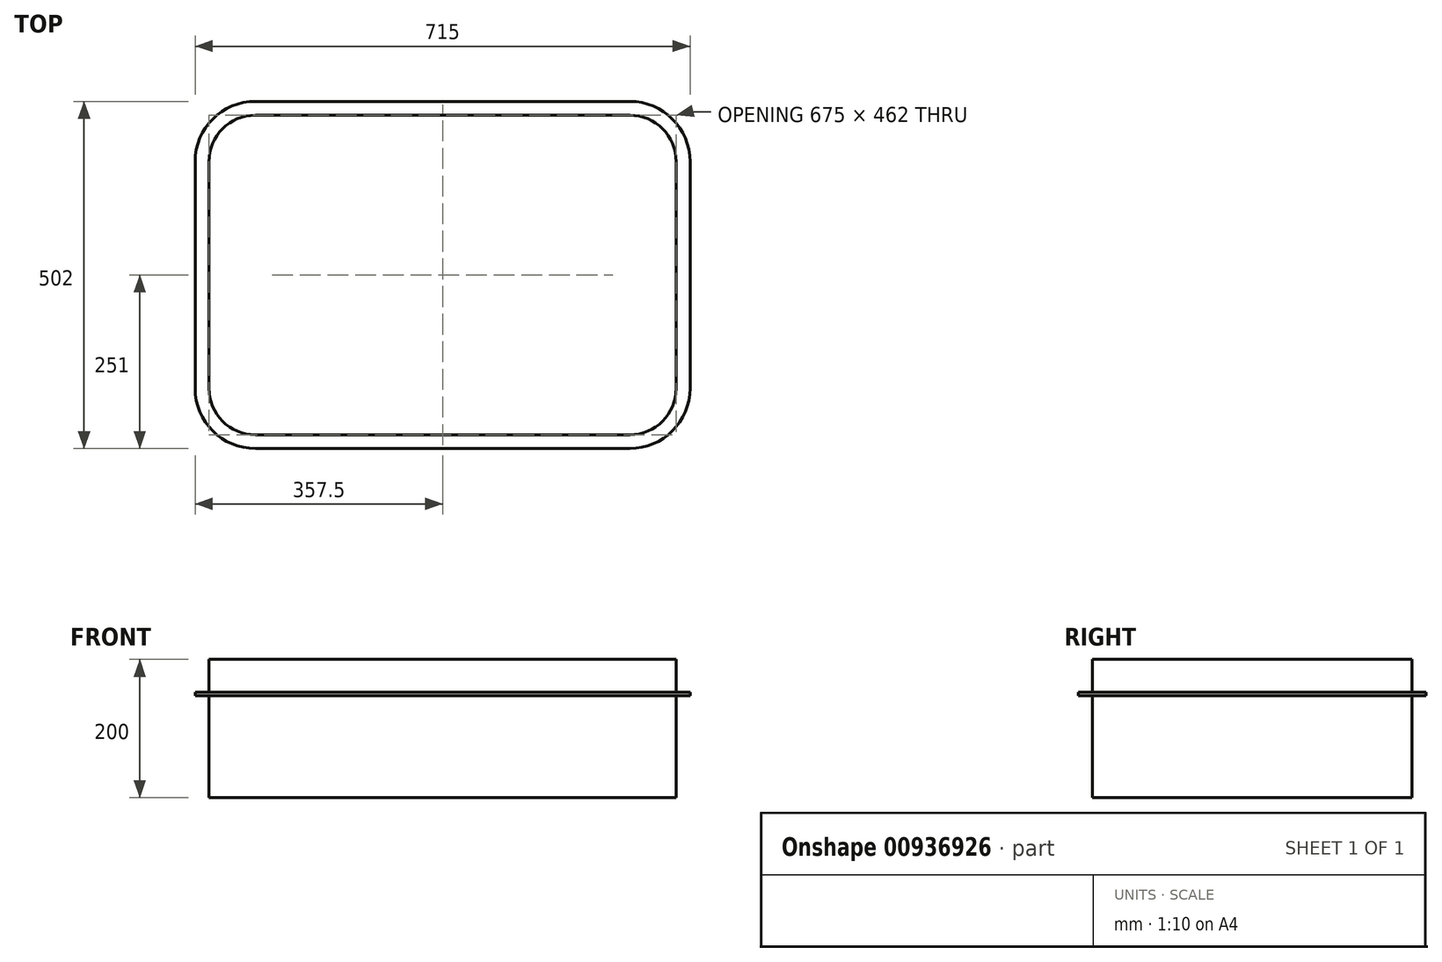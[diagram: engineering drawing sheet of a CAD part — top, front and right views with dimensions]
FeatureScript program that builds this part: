
annotation { "Feature Type Name" : "Feature", "Feature Type Description" : "" }
export const myFeature = defineFeature(function(context is Context, id is Id, definition is map)
    precondition{}
    {
        {
            var Q0;
            Q0=qCreatedBy(makeId("Top.planeOp"),FACE);
            var sketch = newSketch(context, id + "F0", { "sketchPlane" : qUnion([Q0])});
            skLineSegment(sketch, "E0.bottom", {"start": v(270.5, -231) * mm, "end": v(-270.5, -231) * mm});
            skLineSegment(sketch, "E0.top", {"start": v(270.5, 231) * mm, "end": v(-270.5, 231) * mm});
            skLineSegment(sketch, "E0.left", {"start": v(337.5, -164) * mm, "end": v(337.5, 164) * mm});
            skLineSegment(sketch, "E0.right", {"start": v(-337.5, -164) * mm, "end": v(-337.5, 164) * mm});
            skPoint(sketch, "E0.middle", {"position": v(0, 0) * mm});
            skLineSegment(sketch, "E1.bottom", {"start": v(270.5, -251) * mm, "end": v(-270.5, -251) * mm});
            skLineSegment(sketch, "E1.top", {"start": v(270.5, 251) * mm, "end": v(-270.5, 251) * mm});
            skLineSegment(sketch, "E1.left", {"start": v(357.5, -164) * mm, "end": v(357.5, 164) * mm});
            skLineSegment(sketch, "E1.right", {"start": v(-357.5, -164) * mm, "end": v(-357.5, 164) * mm});
            skPoint(sketch, "E2.visualSharp", {"position": v(-337.5, 231) * mm});
            skArc(sketch, "E2.filletArc", {"start": v(-270.5, 231) * mm, "mid": v(-317.88, 211.38) * mm, "end": v(-337.5, 164) * mm});
            skPoint(sketch, "E3.visualSharp", {"position": v(337.5, 231) * mm});
            skArc(sketch, "E3.filletArc", {"start": v(337.5, 164) * mm, "mid": v(317.88, 211.38) * mm, "end": v(270.5, 231) * mm});
            skPoint(sketch, "E4.visualSharp", {"position": v(337.5, -231) * mm});
            skArc(sketch, "E4.filletArc", {"start": v(270.5, -231) * mm, "mid": v(317.88, -211.38) * mm, "end": v(337.5, -164) * mm});
            skPoint(sketch, "E5.visualSharp", {"position": v(-337.5, -231) * mm});
            skArc(sketch, "E5.filletArc", {"start": v(-337.5, -164) * mm, "mid": v(-317.88, -211.38) * mm, "end": v(-270.5, -231) * mm});
            skPoint(sketch, "E6.visualSharp", {"position": v(-357.5, 251) * mm});
            skArc(sketch, "E6.filletArc", {"start": v(-270.5, 251) * mm, "mid": v(-332.02, 225.52) * mm, "end": v(-357.5, 164) * mm});
            skPoint(sketch, "E7.visualSharp", {"position": v(357.5, 251) * mm});
            skArc(sketch, "E7.filletArc", {"start": v(357.5, 164) * mm, "mid": v(332.02, 225.52) * mm, "end": v(270.5, 251) * mm});
            skPoint(sketch, "E8.visualSharp", {"position": v(357.5, -251) * mm});
            skArc(sketch, "E8.filletArc", {"start": v(270.5, -251) * mm, "mid": v(332.02, -225.52) * mm, "end": v(357.5, -164) * mm});
            skPoint(sketch, "E9.visualSharp", {"position": v(-357.5, -251) * mm});
            skArc(sketch, "E9.filletArc", {"start": v(-357.5, -164) * mm, "mid": v(-332.02, -225.52) * mm, "end": v(-270.5, -251) * mm});
            skSolve(sketch);
        }
        {
            var Q0;
            Q0=makeQuery(id+"F0.imprint","IMPRINT",FACE,{"disambiguationData":[TD([[makeQuery(id+"F0.imprint","IMPRINT",EDGE,{"derivedFrom":sQuery(id+"F0.wireOp",EDGE,"E0.bottom")}),1.0]])]});
            extrude(context, id + "F1", {"entities" : qUnion([Q0]), "endBound" : BoundingType.SYMMETRIC, "depth" : 5 * mm, "offsetDistance" : 25 * mm});
        }
        {
            var Q0;
            Q0=makeQuery(id+"F0.imprint","IMPRINT",FACE,{"disambiguationData":[TD([[makeQuery(id+"F0.imprint","IMPRINT",EDGE,{"derivedFrom":sQuery(id+"F0.wireOp",EDGE,"E0.bottom")}),-1.0]])]});
            extrude(context, id + "F2", {"entities" : qUnion([Q0]), "operationType" : NewBodyOperationType.ADD, "depth" : 50 * mm, "offsetDistance" : 25 * mm});
        }
        {
            var Q0;
            Q0=makeQuery(id+"F0.imprint","IMPRINT",FACE,{"disambiguationData":[TD([[makeQuery(id+"F0.imprint","IMPRINT",EDGE,{"derivedFrom":sQuery(id+"F0.wireOp",EDGE,"E0.bottom")}),-1.0]])]});
            extrude(context, id + "F3", {"entities" : qUnion([Q0]), "operationType" : NewBodyOperationType.ADD, "oppositeDirection" : true, "depth" : 150 * mm, "offsetDistance" : 25 * mm});
        }
    });
